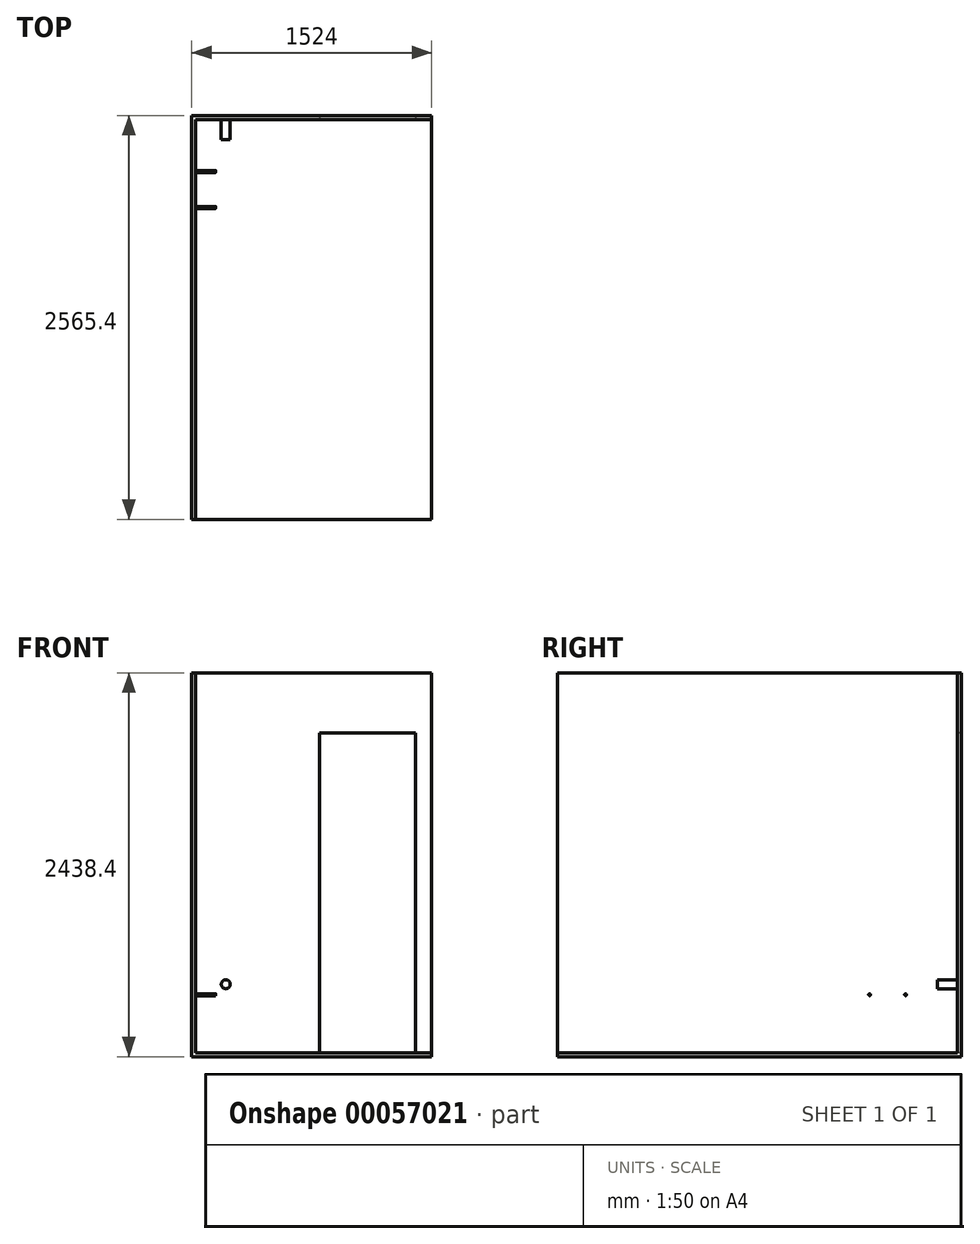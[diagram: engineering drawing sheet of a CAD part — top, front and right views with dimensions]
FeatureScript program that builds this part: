
annotation { "Feature Type Name" : "Feature", "Feature Type Description" : "" }
export const myFeature = defineFeature(function(context is Context, id is Id, definition is map)
    precondition{}
    {
        {
            var Q0;
            Q0=qCreatedBy(makeId("Top.planeOp"),FACE);
            var sketch = newSketch(context, id + "F0", { "sketchPlane" : qUnion([Q0])});
            skLineSegment(sketch, "E0.bottom", {"start": v(-751.5, 1980.05) * mm, "end": v(747.1, 1980.05) * mm});
            skLineSegment(sketch, "E0.top", {"start": v(-751.5, -559.95) * mm, "end": v(747.1, -559.95) * mm});
            skLineSegment(sketch, "E0.left", {"start": v(-751.5, 1980.05) * mm, "end": v(-751.5, -559.95) * mm});
            skLineSegment(sketch, "E0.right", {"start": v(747.1, 1980.05) * mm, "end": v(747.1, -559.95) * mm});
            skSolve(sketch);
        }
        {
            var Q0;
            Q0 = qSketchRegion(id + "F0", true);
            extrude(context, id + "F1", {"entities" : qUnion([Q0]), "depth" : 25.4 * mm});
        }
        {
            var Q0;
            Q0=makeQuery(id+"F1.opExtrude","SWEPT_FACE",FACE,{"disambiguationData":[OSD([sQuery(id+"F0.wireOp",EDGE,"E0.left")])]});
            var sketch = newSketch(context, id + "F2", { "sketchPlane" : qUnion([Q0])});
            skLineSegment(sketch, "E1.bottom", {"start": v(-1980.05, 0) * mm, "end": v(559.95, 0) * mm});
            skLineSegment(sketch, "E1.top", {"start": v(-1980.05, 2438.4) * mm, "end": v(559.95, 2438.4) * mm});
            skLineSegment(sketch, "E1.left", {"start": v(-1980.05, 0) * mm, "end": v(-1980.05, 2438.4) * mm});
            skLineSegment(sketch, "E1.right", {"start": v(559.95, 0) * mm, "end": v(559.95, 2438.4) * mm});
            skSolve(sketch);
        }
        {
            var Q0;
            Q0 = qSketchRegion(id + "F2", true);
            extrude(context, id + "F3", {"entities" : qUnion([Q0]), "operationType" : NewBodyOperationType.ADD, "depth" : 25.4 * mm});
        }
        {
            var Q0;
            Q0=makeQuery(id+"F3.opExtrude","CAP_FACE",FACE,{"disambiguationData":[OSD([sQuery(id+"F2.wireOp",EDGE,"E1.bottom"),sQuery(id+"F2.wireOp",EDGE,"E1.top"),sQuery(id+"F2.wireOp",EDGE,"E1.left"),sQuery(id+"F2.wireOp",EDGE,"E1.right")])],"isStart":true});
            var sketch = newSketch(context, id + "F4", { "sketchPlane" : qUnion([Q0])});
            skCircle(sketch, "E2", {"center": v(1649.85, 393.7) * mm, "radius": 6.35 * mm});
            skCircle(sketch, "E3", {"center": v(1421.25, 393.7) * mm, "radius": 6.35 * mm});
            skSolve(sketch);
        }
        {
            var Q0;
            Q0 = qSketchRegion(id + "F4", true);
            extrude(context, id + "F5", {"entities" : qUnion([Q0]), "operationType" : NewBodyOperationType.ADD, "depth" : 127 * mm});
        }
        {
            var Q0;
            Q0=makeQuery(id+"F3.boolean.opBoolean","MERGE",FACE,{"derivedFrom":[makeQuery(id+"F1.opExtrude","SWEPT_FACE",FACE,{"disambiguationData":[OSD([sQuery(id+"F0.wireOp",EDGE,"E0.bottom")])]}),makeQuery(id+"F3.opExtrude","SWEPT_FACE",FACE,{"disambiguationData":[OSD([sQuery(id+"F2.wireOp",EDGE,"E1.left")])]})]});
            var sketch = newSketch(context, id + "F6", { "sketchPlane" : qUnion([Q0])});
            skLineSegment(sketch, "E4.bottom", {"start": v(776.9, 0) * mm, "end": v(-747.1, 0) * mm});
            skLineSegment(sketch, "E4.top", {"start": v(776.9, 2438.4) * mm, "end": v(-747.1, 2438.4) * mm});
            skLineSegment(sketch, "E4.left", {"start": v(776.9, 0) * mm, "end": v(776.9, 2438.4) * mm});
            skLineSegment(sketch, "E4.right", {"start": v(-747.1, 0) * mm, "end": v(-747.1, 2438.4) * mm});
            skSolve(sketch);
        }
        {
            var Q0;
            Q0 = qSketchRegion(id + "F6", true);
            extrude(context, id + "F7", {"entities" : qUnion([Q0]), "operationType" : NewBodyOperationType.ADD, "depth" : 25.4 * mm});
        }
        {
            var Q0;
            Q0=makeQuery(id+"F7.opExtrude","CAP_FACE",FACE,{"disambiguationData":[OSD([sQuery(id+"F6.wireOp",EDGE,"E4.bottom"),sQuery(id+"F6.wireOp",EDGE,"E4.top"),sQuery(id+"F6.wireOp",EDGE,"E4.left"),sQuery(id+"F6.wireOp",EDGE,"E4.right")])],"isStart":true});
            var sketch = newSketch(context, id + "F8", { "sketchPlane" : qUnion([Q0])});
            skCircle(sketch, "E5", {"center": v(-561, 460.38) * mm, "radius": 28.58 * mm});
            skSolve(sketch);
        }
        {
            var Q0;
            Q0 = qSketchRegion(id + "F8", true);
            extrude(context, id + "F9", {"entities" : qUnion([Q0]), "operationType" : NewBodyOperationType.ADD, "depth" : 127 * mm});
        }
        {
            var Q0;
            Q0=makeQuery(id+"F7.opExtrude","CAP_FACE",FACE,{"disambiguationData":[OSD([sQuery(id+"F6.wireOp",EDGE,"E4.bottom"),sQuery(id+"F6.wireOp",EDGE,"E4.top"),sQuery(id+"F6.wireOp",EDGE,"E4.left"),sQuery(id+"F6.wireOp",EDGE,"E4.right")])],"isStart":true});
            var sketch = newSketch(context, id + "F10", { "sketchPlane" : qUnion([Q0])});
            skLineSegment(sketch, "E6.bottom", {"start": v(645.5, 25.4) * mm, "end": v(35.9, 25.4) * mm});
            skLineSegment(sketch, "E6.top", {"start": v(645.5, 2057.4) * mm, "end": v(35.9, 2057.4) * mm});
            skLineSegment(sketch, "E6.left", {"start": v(645.5, 25.4) * mm, "end": v(645.5, 2057.4) * mm});
            skLineSegment(sketch, "E6.right", {"start": v(35.9, 25.4) * mm, "end": v(35.9, 2057.4) * mm});
            skSolve(sketch);
        }
        {
            var Q0;
            Q0 = qSketchRegion(id + "F10", true);
            extrude(context, id + "F11", {"entities" : qUnion([Q0]), "operationType" : NewBodyOperationType.REMOVE, "endBound" : BoundingType.SYMMETRIC, "oppositeDirection" : true, "depth" : 76.2 * mm});
        }
    });
